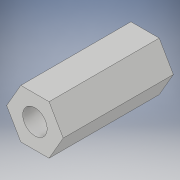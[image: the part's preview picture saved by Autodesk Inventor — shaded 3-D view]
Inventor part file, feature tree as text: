
AUTODESK INVENTOR PART (.ipt)
format: ipt  version: 2018 (Build 220112000, 112)  size: 96,256 bytes
history: native  units: in
note: dims shown in document units (in); Inventor stores cm internally (conversion verified against a paired STEP export)
features: extrude x1, sketch x1
ambient origin geometry x8: Origin, YZ Plane, XZ Plane, XY Plane, X Axis, Y Axis, Z Axis, Center Point
bodies: Solid1 (feature_tree)
feature tree (2):
  extrude  "Extrusion1"  Depth=1.125in
  sketch  "Sketch1"  dims[d0=0.5in d1=0.25in d2=1.125in d3=0.0in]
